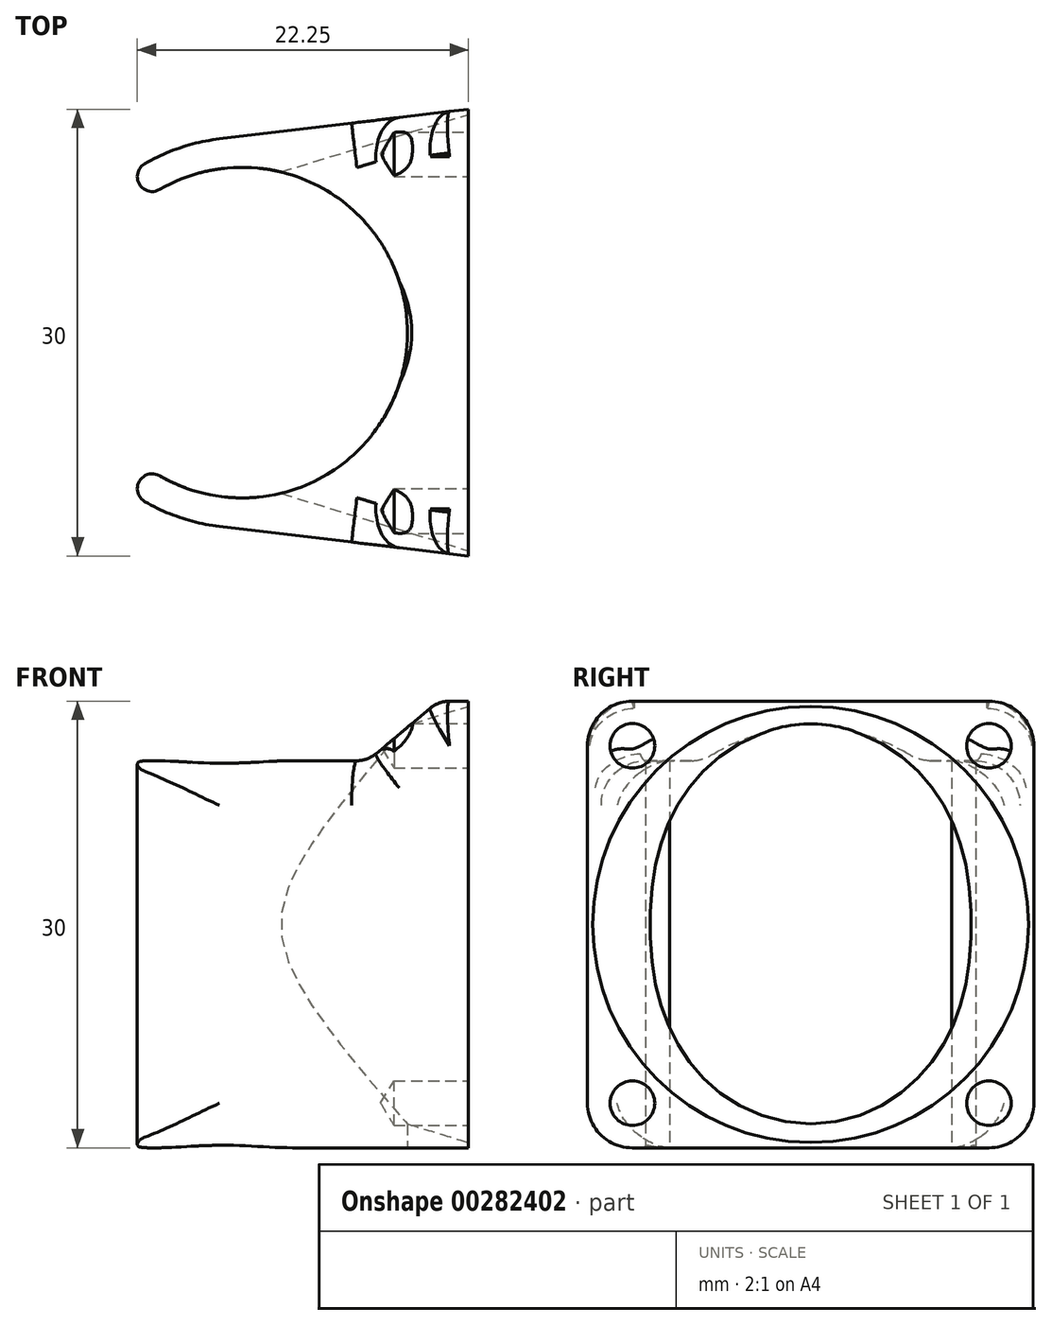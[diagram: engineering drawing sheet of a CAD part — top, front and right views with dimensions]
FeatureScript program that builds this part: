
annotation { "Feature Type Name" : "Feature", "Feature Type Description" : "" }
export const myFeature = defineFeature(function(context is Context, id is Id, definition is map)
    precondition{}
    {
        {
            var Q0;
            Q0=qCreatedBy(makeId("Top.planeOp"),FACE);
            var sketch = newSketch(context, id + "F0", { "sketchPlane" : qUnion([Q0])});
            skArc(sketch, "E0", {"start": v(-5.55, -9.61) * mm, "mid": v(11.1, 0) * mm, "end": v(-5.55, 9.61) * mm});
            skLineSegment(sketch, "E1", {"start": v(0, 0) * mm, "end": v(-11.1, 0) * mm, "construction": true});
            skLineSegment(sketch, "E2", {"start": v(0, 0) * mm, "end": v(-6.55, 11.34) * mm, "construction": true});
            skLineSegment(sketch, "E3", {"start": v(0, 0) * mm, "end": v(-6.55, -11.34) * mm, "construction": true});
            skLineSegment(sketch, "E4", {"start": v(15.2, 15) * mm, "end": v(15.2, -15) * mm});
            skArc(sketch, "E5.0", {"start": v(-1.55, 13) * mm, "mid": v(-4.13, 12.43) * mm, "end": v(-6.55, 11.34) * mm});
            skLineSegment(sketch, "E6", {"start": v(15.2, 15) * mm, "end": v(-1.55, 13) * mm});
            skLineSegment(sketch, "E7", {"start": v(15.2, -15) * mm, "end": v(-1.55, -13) * mm});
            skArc(sketch, "E8.trimOffspring", {"start": v(-6.55, -11.34) * mm, "mid": v(-4.13, -12.43) * mm, "end": v(-1.55, -13) * mm});
            skArc(sketch, "E9", {"start": v(-6.55, 11.34) * mm, "mid": v(-6.92, 9.98) * mm, "end": v(-5.55, 9.61) * mm});
            skArc(sketch, "E10", {"start": v(-5.55, -9.61) * mm, "mid": v(-6.92, -9.98) * mm, "end": v(-6.55, -11.34) * mm});
            skSolve(sketch);
        }
        {
            var Q0;
            Q0=qSketchRegion(id+"F0",true);
            extrude(context, id + "F1", {"entities" : qUnion([Q0]), "depth" : 30 * mm});
        }
        {
            var Q0;
            Q0=qCreatedBy(makeId("Right.planeOp"),FACE);
            var sketch = newSketch(context, id + "F2", { "sketchPlane" : qUnion([Q0])});
            skLineSegment(sketch, "E11", {"start": v(0, 0) * mm, "end": v(0, 15) * mm, "construction": true});
            skCircle(sketch, "E12", {"center": v(0, 15) * mm, "radius": 10 * mm});
            skSolve(sketch);
        }
        {
            var Q0;
            Q0=qSketchRegion(id+"F2",true);
            extrude(context, id + "F3", {"entities" : qUnion([Q0]), "operationType" : NewBodyOperationType.REMOVE, "depth" : 20 * mm, "hasDraft" : true, "draftAngle" : 17 * degree});
        }
        {
            var Q0;
            Q0=qCreatedBy(makeId("Front.planeOp"),FACE);
            var sketch = newSketch(context, id + "F4", { "sketchPlane" : qUnion([Q0])});
            skLineSegment(sketch, "E13", {"start": v(0, 0) * mm, "end": v(0, 26) * mm, "construction": true});
            skLineSegment(sketch, "E14", {"start": v(0, 26) * mm, "end": v(7.7, 26) * mm});
            skLineSegment(sketch, "E15", {"start": v(9, 26.47) * mm, "end": v(12.64, 29.53) * mm});
            skLineSegment(sketch, "E16", {"start": v(13.93, 30) * mm, "end": v(15.2, 30) * mm});
            skLineSegment(sketch, "E17", {"start": v(0, 26) * mm, "end": v(-8, 26) * mm});
            skPoint(sketch, "E18.visualSharp", {"position": v(8.43, 26) * mm});
            skArc(sketch, "E18.filletArc", {"start": v(7.7, 26) * mm, "mid": v(8.39, 26.12) * mm, "end": v(9, 26.47) * mm});
            skPoint(sketch, "E19.visualSharp", {"position": v(13.2, 30) * mm});
            skArc(sketch, "E19.filletArc", {"start": v(13.93, 30) * mm, "mid": v(13.24, 29.88) * mm, "end": v(12.64, 29.53) * mm});
            skLineSegment(sketch, "E20", {"start": v(15.2, 30) * mm, "end": v(15.2, 32) * mm});
            skLineSegment(sketch, "E21", {"start": v(15.2, 32) * mm, "end": v(-8, 32) * mm});
            skLineSegment(sketch, "E22", {"start": v(-8, 32) * mm, "end": v(-8, 26) * mm});
            skSolve(sketch);
        }
        {
            var Q0;
            Q0=qSketchRegion(id+"F4",true);
            extrude(context, id + "F5", {"entities" : qUnion([Q0]), "operationType" : NewBodyOperationType.REMOVE, "oppositeDirection" : true, "depth" : 25 * mm});
        }
        {
            var Q0;
            Q0=qSketchRegion(id+"F4",true);
            extrude(context, id + "F6", {"entities" : qUnion([Q0]), "operationType" : NewBodyOperationType.REMOVE, "depth" : 25 * mm});
        }
        {
            var Q0;
            Q0=makeQuery(id+"F1.opExtrude","CAP_EDGE",EDGE,{"disambiguationData":[OSD([sQuery(id+"F0.wireOp",EDGE,"E7")])],"isStart":false});
            var Q1;
            Q1=makeQuery(id+"F6.boolean.opBoolean","INTERSECT",EDGE,{"derivedFrom":[makeQuery(id+"F1.opExtrude","SWEPT_FACE",FACE,{"disambiguationData":[OSD([sQuery(id+"F0.wireOp",EDGE,"E7")])]}),makeQuery(id+"F6.opExtrude","SWEPT_FACE",FACE,{"disambiguationData":[OSD([sQuery(id+"F4.wireOp",EDGE,"E19.filletArc")])]})]});
            var Q2;
            Q2=makeQuery(id+"F6.boolean.opBoolean","INTERSECT",EDGE,{"derivedFrom":[makeQuery(id+"F1.opExtrude","SWEPT_FACE",FACE,{"disambiguationData":[OSD([sQuery(id+"F0.wireOp",EDGE,"E7")])]}),makeQuery(id+"F6.opExtrude","SWEPT_FACE",FACE,{"disambiguationData":[OSD([sQuery(id+"F4.wireOp",EDGE,"E15")])]})]});
            var Q3;
            Q3=makeQuery(id+"F6.boolean.opBoolean","INTERSECT",EDGE,{"derivedFrom":[makeQuery(id+"F1.opExtrude","SWEPT_FACE",FACE,{"disambiguationData":[OSD([sQuery(id+"F0.wireOp",EDGE,"E7")])]}),makeQuery(id+"F6.opExtrude","SWEPT_FACE",FACE,{"disambiguationData":[OSD([sQuery(id+"F4.wireOp",EDGE,"E18.filletArc")])]})]});
            var Q4;
            Q4=makeQuery(id+"F6.boolean.opBoolean","INTERSECT",EDGE,{"derivedFrom":[makeQuery(id+"F1.opExtrude","SWEPT_FACE",FACE,{"disambiguationData":[OSD([sQuery(id+"F0.wireOp",EDGE,"E7")])]}),makeQuery(id+"F6.opExtrude","SWEPT_FACE",FACE,{"disambiguationData":[OSD([sQuery(id+"F4.wireOp",EDGE,"E14"),sQuery(id+"F4.wireOp",EDGE,"E17")])]})]});
            var Q5;
            Q5=makeQuery(id+"F1.opExtrude","CAP_EDGE",EDGE,{"disambiguationData":[OSD([sQuery(id+"F0.wireOp",EDGE,"E6")])],"isStart":false});
            var Q6;
            Q6=makeQuery(id+"F5.boolean.opBoolean","INTERSECT",EDGE,{"derivedFrom":[makeQuery(id+"F1.opExtrude","SWEPT_FACE",FACE,{"disambiguationData":[OSD([sQuery(id+"F0.wireOp",EDGE,"E6")])]}),makeQuery(id+"F5.opExtrude","SWEPT_FACE",FACE,{"disambiguationData":[OSD([sQuery(id+"F4.wireOp",EDGE,"E19.filletArc")])]})]});
            var Q7;
            Q7=makeQuery(id+"F5.boolean.opBoolean","INTERSECT",EDGE,{"derivedFrom":[makeQuery(id+"F1.opExtrude","SWEPT_FACE",FACE,{"disambiguationData":[OSD([sQuery(id+"F0.wireOp",EDGE,"E6")])]}),makeQuery(id+"F5.opExtrude","SWEPT_FACE",FACE,{"disambiguationData":[OSD([sQuery(id+"F4.wireOp",EDGE,"E15")])]})]});
            var Q8;
            Q8=makeQuery(id+"F5.boolean.opBoolean","INTERSECT",EDGE,{"derivedFrom":[makeQuery(id+"F1.opExtrude","SWEPT_FACE",FACE,{"disambiguationData":[OSD([sQuery(id+"F0.wireOp",EDGE,"E6")])]}),makeQuery(id+"F5.opExtrude","SWEPT_FACE",FACE,{"disambiguationData":[OSD([sQuery(id+"F4.wireOp",EDGE,"E18.filletArc")])]})]});
            var Q9;
            Q9=makeQuery(id+"F5.boolean.opBoolean","INTERSECT",EDGE,{"derivedFrom":[makeQuery(id+"F1.opExtrude","SWEPT_FACE",FACE,{"disambiguationData":[OSD([sQuery(id+"F0.wireOp",EDGE,"E6")])]}),makeQuery(id+"F5.opExtrude","SWEPT_FACE",FACE,{"disambiguationData":[OSD([sQuery(id+"F4.wireOp",EDGE,"E14"),sQuery(id+"F4.wireOp",EDGE,"E17")])]})]});
            var Q10;
            Q10=makeQuery(id+"F1.opExtrude","CAP_EDGE",EDGE,{"disambiguationData":[OSD([sQuery(id+"F0.wireOp",EDGE,"E7")])],"isStart":true});
            var Q11;
            Q11=makeQuery(id+"F1.opExtrude","CAP_EDGE",EDGE,{"disambiguationData":[OSD([sQuery(id+"F0.wireOp",EDGE,"E6")])],"isStart":true});
            fillet(context, id + "F7", {"entities" : qUnion([Q0, Q1, Q2, Q3, Q4, Q5, Q6, Q7, Q8, Q9, Q10, Q11]), "radius" : 3 * mm, "allowEdgeOverflow" : false});
        }
        {
            var Q0;
            Q0=makeQuery(id+"F1.opExtrude","SWEPT_FACE",FACE,{"disambiguationData":[OSD([sQuery(id+"F0.wireOp",EDGE,"E4")])]});
            var sketch = newSketch(context, id + "F8", { "sketchPlane" : qUnion([Q0])});
            skPoint(sketch, "E23", {"position": v(-11.98, 3) * mm});
            skPoint(sketch, "E24", {"position": v(11.98, 3) * mm});
            skPoint(sketch, "E25", {"position": v(11.98, 27) * mm});
            skPoint(sketch, "E26", {"position": v(-11.98, 27) * mm});
            skSolve(sketch);
        }
        {
            var Q0;
            Q0=sQuery(id+"F8.wireOp",VERTEX,"E26");
            var Q1;
            Q1=sQuery(id+"F8.wireOp",VERTEX,"E25");
            var Q2;
            Q2=sQuery(id+"F8.wireOp",VERTEX,"E24");
            var Q3;
            Q3=sQuery(id+"F8.wireOp",VERTEX,"E23");
            var Q4;
            Q4=makeQuery(id+"F1.opExtrude","SWEPT_BODY",BODY,{"disambiguationData":[OSD([sQuery(id+"F0.wireOp",EDGE,"E0"),sQuery(id+"F0.wireOp",EDGE,"E4"),sQuery(id+"F0.wireOp",EDGE,"E5.0"),sQuery(id+"F0.wireOp",EDGE,"E6"),sQuery(id+"F0.wireOp",EDGE,"E7"),sQuery(id+"F0.wireOp",EDGE,"E8.trimOffspring"),sQuery(id+"F0.wireOp",EDGE,"E9"),sQuery(id+"F0.wireOp",EDGE,"E10")])]});
            hole(context, id + "F9", {"style" : HoleStyle.SIMPLE, "endStyle" : HoleEndStyle.BLIND, "standardTappedOrClearance" : lookupTablePath({ "standard" : "ISO", "size" : "3", "type" : "Drilled" }), "standardBlindInLast" : lookupTablePath({ "standard" : "ISO", "size" : "3", "type" : "Drilled" }), "holeDiameter" : 3 * mm, "holeDepth" : 5 * mm, "startFromSketch" : true, "locations" : qUnion([Q0, Q1, Q2, Q3]), "scope" : qUnion([Q4])});
        }
    });
